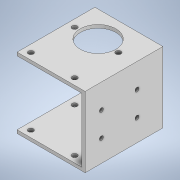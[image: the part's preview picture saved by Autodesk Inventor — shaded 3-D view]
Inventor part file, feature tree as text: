
AUTODESK INVENTOR PART (.ipt)
format: ipt  version: 2022 (Build 260153000, 153)  size: 168,448 bytes
history: native  units: mm
features: sketch x6, hole x4, extrude x2, other x1
ambient origin geometry x8: Origin, YZ Plane, XZ Plane, XY Plane, X Axis, Y Axis, Z Axis, Center Point
bodies: Body1 (feature_tree)
feature tree (13):
  other  "ソリッド1"
  extrude  "押し出し1"  Depth=48.0mm
  extrude  "押し出し2"  Depth=42.0mm
  hole  "穴1"  [1 undecoded]
  hole  "穴2"  [1 undecoded]
  hole  "穴3"  [1 undecoded]
  hole  "穴4"  [1 undecoded]
  sketch  "スケッチ1"
  sketch  "スケッチ2"
  sketch  "スケッチ3"
  sketch  "スケッチ4"
  sketch  "スケッチ5"
  sketch  "スケッチ6"
note: 4 required parameter values undecoded (feature->parameter linkage not recoverable at this tier; creation-order binding heuristic only, values carry confidence <= 0.55)
